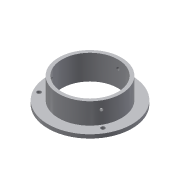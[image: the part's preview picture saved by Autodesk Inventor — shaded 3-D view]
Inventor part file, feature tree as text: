
AUTODESK INVENTOR PART (.ipt)
format: ipt  version: 2016 (Build 200138000, 138)  size: 195,072 bytes
history: native  units: in
note: dims shown in document units (in); Inventor stores cm internally (conversion verified against a paired STEP export)
features: sketch x6, extrude x2, hole x2, pattern_circular x2, plane x1
ambient origin geometry x8: Origin, YZ Plane, XZ Plane, XY Plane, X Axis, Y Axis, Z Axis, Center Point
bodies: Solid1 (feature_tree), body (feature_tree)
feature tree (13):
  extrude  "hole"  Depth=1.5748in TaperAngle=0.0deg
  extrude  "flange"  Depth=4.0in TaperAngle=0.0deg
  sketch  "Sketch4"  dims[d12=0.5118in]
  plane  "Work Plane1"
  hole  "sideHoleSE"  [1 undecoded]
  pattern_circular  "sideHoleSW"  Count=2 Angle=120.0deg
  pattern_circular  "sideHoleN"  Count=2 Angle=120.0deg
  hole  "Hole5"  [1 undecoded]
  sketch  "Sketch1"  dims[d0=5.315in d2=1.5748in d3=0.0in]
  sketch  "Sketch2"  dims[d4=3.55in d6=4.0in d7=0.0in]
  sketch  "Sketch3"  dims[d9=0.2126in d10=1.3386in d11=0.0in]
  sketch  "Sketch5"  dims[d13=0.2in]
  sketch  "Sketch8"  dims[d14=0.1936in d15=0.4724in d16=0.375in d17=0.25in d18=0.5635in d19=0.6732in d20=0.8108in d59=0.7874in d60=120.0deg d62=0.7874in d63=120.0deg d65=2.2441in d66=2.2441in d67=30.0deg d68=2.3622in d69=150.0deg d70=0.2598in d71=0.2362in d72=0.4961in d73=0.0787in d74=90.0deg d75=0.315in d76=0.8108in]
note: 2 required parameter values undecoded (feature->parameter linkage not recoverable at this tier; creation-order binding heuristic only, values carry confidence <= 0.55)
